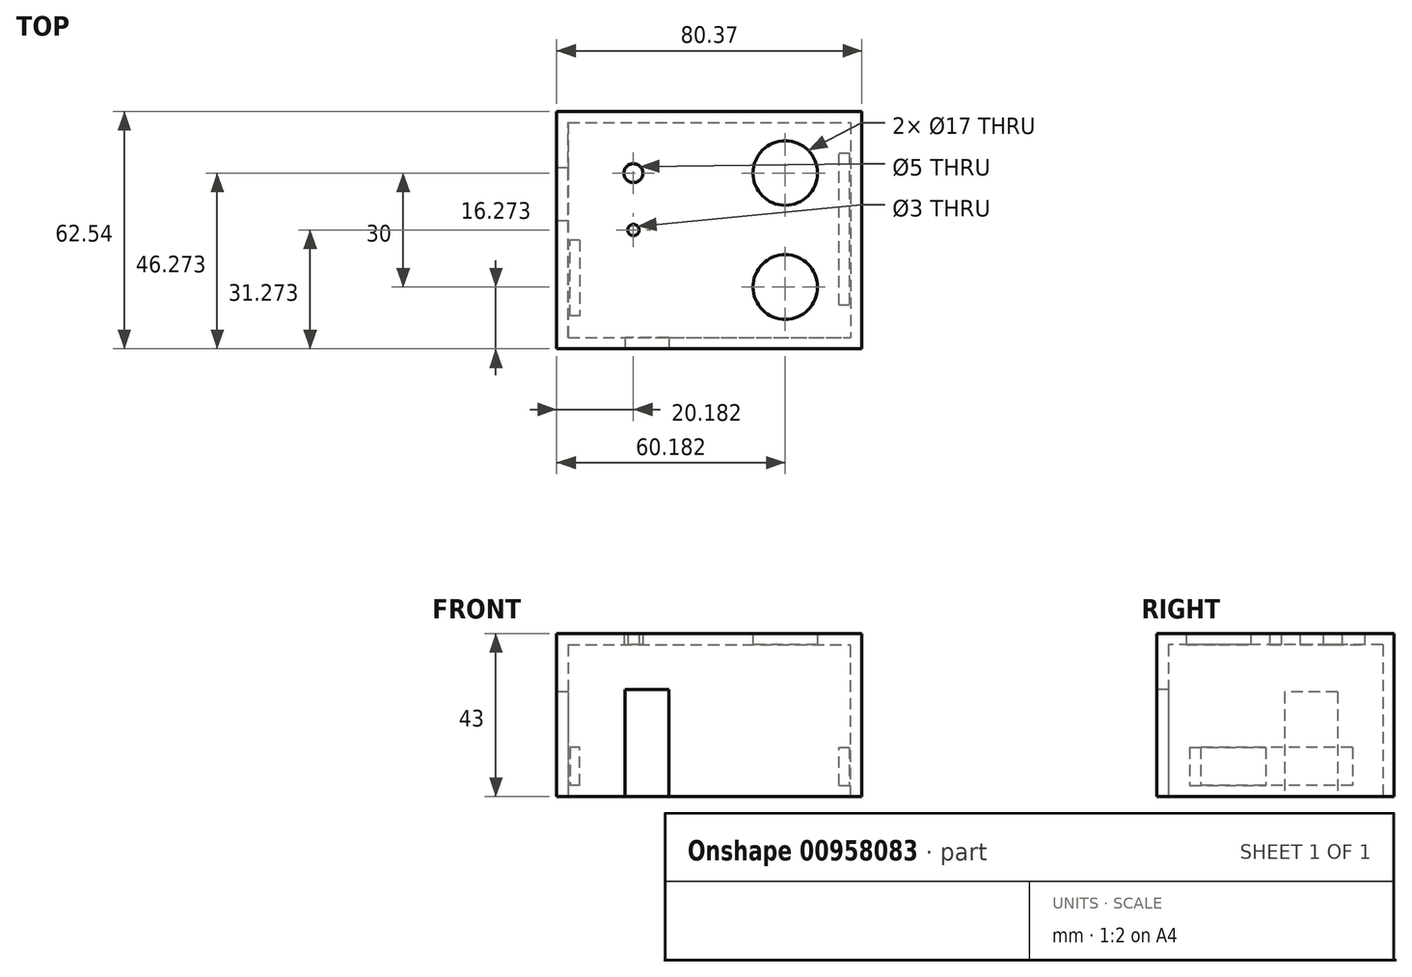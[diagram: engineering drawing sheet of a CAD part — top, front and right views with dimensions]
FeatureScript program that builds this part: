
annotation { "Feature Type Name" : "Feature", "Feature Type Description" : "" }
export const myFeature = defineFeature(function(context is Context, id is Id, definition is map)
    precondition{}
    {
        {
            var Q0;
            Q0=qCreatedBy(makeId("Top.planeOp"),FACE);
            var sketch = newSketch(context, id + "F0", { "sketchPlane" : qUnion([Q0])});
            skLineSegment(sketch, "E0.bottom", {"start": v(-70.32, 44.73) * mm, "end": v(10.05, 44.73) * mm});
            skLineSegment(sketch, "E0.top", {"start": v(-70.32, -17.8) * mm, "end": v(10.05, -17.8) * mm});
            skLineSegment(sketch, "E0.left", {"start": v(-70.32, 44.73) * mm, "end": v(-70.32, -17.8) * mm});
            skLineSegment(sketch, "E0.right", {"start": v(10.05, 44.73) * mm, "end": v(10.05, -17.8) * mm});
            skLineSegment(sketch, "E1", {"start": v(-30.14, 44.73) * mm, "end": v(-30.14, -17.8) * mm});
            skLineSegment(sketch, "E2", {"start": v(-70.32, 13.46) * mm, "end": v(10.05, 13.46) * mm});
            skLineSegment(sketch, "E3", {"start": v(-10.14, 44.73) * mm, "end": v(-10.14, -17.8) * mm});
            skLineSegment(sketch, "E4", {"start": v(-50.14, 44.73) * mm, "end": v(-50.14, -17.8) * mm});
            skLineSegment(sketch, "E5", {"start": v(-70.32, 28.46) * mm, "end": v(10.05, 28.46) * mm});
            skLineSegment(sketch, "E6", {"start": v(10.05, -1.54) * mm, "end": v(-70.32, -1.54) * mm});
            skCircle(sketch, "E7", {"center": v(-10.14, -1.54) * mm, "radius": 8.5 * mm});
            skCircle(sketch, "E8", {"center": v(-50.14, 28.46) * mm, "radius": 2.5 * mm});
            skCircle(sketch, "E9", {"center": v(-10.14, 28.46) * mm, "radius": 8.5 * mm});
            skCircle(sketch, "E10", {"center": v(-50.14, 13.46) * mm, "radius": 1.5 * mm});
            skSolve(sketch);
        }
        {
            var Q0;
            Q0=qSketchRegion(id+"F0",true);
            var Q1;
            {var subQ0=sQuery(id+"F0.wireOp",EDGE,"E5");var subQ1=sQuery(id+"F0.wireOp",EDGE,"E1");var subQ2=makeQuery(id+"F0.imprint","INTERSECT",VERTEX,{"derivedFrom":[subQ1,subQ0]});Q1=makeQuery(id+"F0.imprint","IMPRINT",FACE,{"disambiguationData":[TD([[makeQuery(id+"F0.imprint","IMPRINT",EDGE,{"disambiguationData":[TD([[subQ2,-1.0]])],"derivedFrom":subQ1}),-1.0]])]});}
            var Q2;
            {var subQ0=sQuery(id+"F0.wireOp",EDGE,"E5");var subQ1=sQuery(id+"F0.wireOp",EDGE,"E1");var subQ2=makeQuery(id+"F0.imprint","INTERSECT",VERTEX,{"derivedFrom":[subQ1,subQ0]});Q2=makeQuery(id+"F0.imprint","IMPRINT",FACE,{"disambiguationData":[TD([[makeQuery(id+"F0.imprint","IMPRINT",EDGE,{"disambiguationData":[TD([[subQ2,-1.0]])],"derivedFrom":subQ1}),1.0]])]});}
            var Q3;
            {var subQ1=sQuery(id+"F0.wireOp",EDGE,"E1");var subQ5=sQuery(id+"F0.wireOp",EDGE,"E2");var subQ6=makeQuery(id+"F0.imprint","INTERSECT",VERTEX,{"derivedFrom":[subQ1,subQ5]});Q3=makeQuery(id+"F0.imprint","IMPRINT",FACE,{"disambiguationData":[TD([[makeQuery(id+"F0.imprint","IMPRINT",EDGE,{"disambiguationData":[TD([[subQ6,-1.0]])],"derivedFrom":subQ1}),1.0]])]});}
            var Q4;
            {var subQ1=sQuery(id+"F0.wireOp",EDGE,"E2");var subQ5=sQuery(id+"F0.wireOp",EDGE,"E1");var subQ6=makeQuery(id+"F0.imprint","INTERSECT",VERTEX,{"derivedFrom":[subQ5,subQ1]});Q4=makeQuery(id+"F0.imprint","IMPRINT",FACE,{"disambiguationData":[TD([[makeQuery(id+"F0.imprint","IMPRINT",EDGE,{"disambiguationData":[TD([[subQ6,-1.0]])],"derivedFrom":subQ5}),-1.0]])]});}
            extrude(context, id + "F1", {"entities" : qUnion([Q0, Q1, Q2, Q3, Q4]), "depth" : 3 * mm, "offsetDistance" : 25 * mm});
        }
        {
            var Q0;
            {var subQ1=sQuery(id+"F0.wireOp",EDGE,"E0.top");var subQ5=sQuery(id+"F0.wireOp",EDGE,"E0.left");var subQ6=makeQuery(id+"F0.imprint","INTERSECT",VERTEX,{"derivedFrom":[subQ1,subQ5]});Q0=makeQuery(id+"F0.imprint","IMPRINT",FACE,{"disambiguationData":[TD([[makeQuery(id+"F0.imprint","IMPRINT",EDGE,{"disambiguationData":[TD([[subQ6,-1.0]])],"derivedFrom":subQ1}),1.0]])]});}
            var sketch = newSketch(context, id + "F2", { "sketchPlane" : qUnion([Q0])});
            skLineSegment(sketch, "E11.0", {"start": v(-67.32, -14.8) * mm, "end": v(7.05, -14.8) * mm});
            skLineSegment(sketch, "E11.1", {"start": v(-67.32, 41.73) * mm, "end": v(-67.32, -14.8) * mm});
            skLineSegment(sketch, "E11.2", {"start": v(-67.32, 41.73) * mm, "end": v(7.05, 41.73) * mm});
            skLineSegment(sketch, "E11.3", {"start": v(7.05, 41.73) * mm, "end": v(7.05, -14.8) * mm});
            skLineSegment(sketch, "E12.0", {"start": v(-70.32, -17.8) * mm, "end": v(10.05, -17.8) * mm});
            skLineSegment(sketch, "E12.1", {"start": v(-70.32, 44.73) * mm, "end": v(-70.32, -17.8) * mm});
            skLineSegment(sketch, "E12.2", {"start": v(-70.32, 44.73) * mm, "end": v(10.05, 44.73) * mm});
            skLineSegment(sketch, "E12.3", {"start": v(10.05, 44.73) * mm, "end": v(10.05, -17.8) * mm});
            skSolve(sketch);
        }
        {
            var Q0;
            {var subQ10=sQuery(id+"F2.wireOp",EDGE,"E11.1");var subQ11=sQuery(id+"F2.wireOp",EDGE,"E11.0");var subQ12=makeQuery(id+"F2.imprint","INTERSECT",VERTEX,{"derivedFrom":[subQ11,subQ10]});Q0=makeQuery(id+"F2.imprint","IMPRINT",FACE,{"disambiguationData":[TD([[makeQuery(id+"F2.imprint","IMPRINT",EDGE,{"disambiguationData":[TD([[subQ12,-1.0]])],"derivedFrom":subQ11}),-1.0]])]});}
            var Q1;
            {var subQ1=sQuery(id+"F2.wireOp",EDGE,"E11.2");Q1=makeQuery(id+"F2.imprint","IMPRINT",FACE,{"disambiguationData":[TD([[makeQuery(id+"F2.imprint","IMPRINT",EDGE,{"derivedFrom":subQ1}),1.0]])]});}
            extrude(context, id + "F3", {"entities" : qUnion([Q0, Q1]), "oppositeDirection" : true, "depth" : 40 * mm, "offsetDistance" : 25 * mm});
        }
        {
            var Q0;
            Q0=makeQuery(id+"F3.boolean.opBoolean","MERGE",FACE,{"derivedFrom":[makeQuery(id+"F1.opExtrude","SWEPT_FACE",FACE,{"disambiguationData":[OSD([sQuery(id+"F0.wireOp",EDGE,"E0.left")])]}),makeQuery(id+"F3.opExtrude","SWEPT_FACE",FACE,{"disambiguationData":[OSD([sQuery(id+"F2.wireOp",EDGE,"E12.1")])]})]});
            var sketch = newSketch(context, id + "F4", { "sketchPlane" : qUnion([Q0])});
            skLineSegment(sketch, "E13.bottom", {"start": v(-29.83, -12.4) * mm, "end": v(-15.83, -12.4) * mm});
            skLineSegment(sketch, "E13.top", {"start": v(-29.83, -29) * mm, "end": v(-15.83, -29) * mm});
            skLineSegment(sketch, "E13.left", {"start": v(-29.83, -12.4) * mm, "end": v(-29.83, -29) * mm});
            skLineSegment(sketch, "E13.right", {"start": v(-15.83, -12.4) * mm, "end": v(-15.83, -29) * mm});
            skLineSegment(sketch, "E14.top", {"start": v(-9.2, -26.4) * mm, "end": v(2.8, -26.4) * mm});
            skLineSegment(sketch, "E14.left", {"start": v(-9.2, -19.4) * mm, "end": v(-9.2, -26.4) * mm});
            skLineSegment(sketch, "E14.right", {"start": v(2.8, -19.4) * mm, "end": v(2.8, -26.4) * mm});
            skLineSegment(sketch, "E15", {"start": v(-9.2, -26.4) * mm, "end": v(-15.83, -26.4) * mm});
            skSolve(sketch);
        }
        {
            var Q0;
            Q0=makeQuery(id+"F4.imprint","IMPRINT",FACE,{"disambiguationData":[TD([[makeQuery(id+"F4.imprint","IMPRINT",EDGE,{"derivedFrom":sQuery(id+"F4.wireOp",EDGE,"E13.bottom")}),-1.0]])]});
            var Q1;
            Q1=makeQuery(id+"F4.imprint","IMPRINT",FACE,{"disambiguationData":[TD([[makeQuery(id+"F4.imprint","IMPRINT",EDGE,{"derivedFrom":sQuery(id+"F4.wireOp",EDGE,"E14.bottom")}),-1.0]])]});
            var Q2;
            Q2=makeQuery(id+"F4.imprint","IMPRINT",FACE,{"disambiguationData":[TD([[makeQuery(id+"F4.imprint","IMPRINT",EDGE,{"derivedFrom":sQuery(id+"F4.wireOp",EDGE,"E14.left")}),-1.0]])]});
            extrude(context, id + "F5", {"entities" : qUnion([Q0, Q1, Q2]), "operationType" : NewBodyOperationType.REMOVE, "oppositeDirection" : true, "depth" : 25 * mm, "offsetDistance" : 25 * mm});
        }
        {
            var Q0;
            Q0=makeQuery(id+"F5.boolean.opBoolean","COPY",FACE,{"derivedFrom":makeQuery(id+"F5.opExtrude","SWEPT_FACE",FACE,{"disambiguationData":[OSD([sQuery(id+"F4.wireOp",EDGE,"E13.top")])]})});
            var Q1;
            Q1=makeQuery(id+"F5.boolean.opBoolean","COPY",FACE,{"derivedFrom":makeQuery(id+"F5.opExtrude","SWEPT_FACE",FACE,{"disambiguationData":[OSD([sQuery(id+"F4.wireOp",EDGE,"E14.top")])]})});
            extrude(context, id + "F6", {"entities" : qUnion([Q0, Q1]), "operationType" : NewBodyOperationType.REMOVE, "endBound" : BoundingType.THROUGH_ALL, "oppositeDirection" : true, "depth" : 25 * mm, "offsetDistance" : 25 * mm});
        }
        {
            var Q0;
            Q0=makeQuery(id+"F3.boolean.opBoolean","MERGE",FACE,{"derivedFrom":[makeQuery(id+"F1.opExtrude","SWEPT_FACE",FACE,{"disambiguationData":[OSD([sQuery(id+"F0.wireOp",EDGE,"E0.top")])]}),makeQuery(id+"F3.opExtrude","SWEPT_FACE",FACE,{"disambiguationData":[OSD([sQuery(id+"F2.wireOp",EDGE,"E12.0")])]})]});
            var sketch = newSketch(context, id + "F7", { "sketchPlane" : qUnion([Q0])});
            skLineSegment(sketch, "E16.bottom", {"start": v(-40.82, -111.8) * mm, "end": v(-52.32, -111.8) * mm});
            skLineSegment(sketch, "E16.top", {"start": v(-40.82, -11.8) * mm, "end": v(-52.32, -11.8) * mm});
            skLineSegment(sketch, "E16.left", {"start": v(-52.32, -11.8) * mm, "end": v(-52.32, -111.8) * mm});
            skLineSegment(sketch, "E16.right", {"start": v(-40.82, -11.8) * mm, "end": v(-40.82, -111.8) * mm});
            skSolve(sketch);
        }
        {
            var Q0;
            Q0=qSketchRegion(id+"F7",true);
            var Q1;
            {var subQ0=sQuery(id+"F7.wireOp",EDGE,"E16.bottom");Q1=makeQuery(id+"F7.imprint","IMPRINT",FACE,{"disambiguationData":[TD([[makeQuery(id+"F7.imprint","IMPRINT",EDGE,{"derivedFrom":subQ0}),-1.0]])]});}
            extrude(context, id + "F8", {"entities" : qUnion([Q0, Q1]), "operationType" : NewBodyOperationType.REMOVE, "oppositeDirection" : true, "depth" : 5.1 * mm, "offsetDistance" : 25 * mm});
        }
        {
            var Q0;
            Q0=makeQuery(id+"F3.opExtrude","SWEPT_FACE",FACE,{"disambiguationData":[OSD([sQuery(id+"F2.wireOp",EDGE,"E11.1")])]});
            var sketch = newSketch(context, id + "F9", { "sketchPlane" : qUnion([Q0])});
            skLineSegment(sketch, "E17.bottom", {"start": v(10.83, -37) * mm, "end": v(-9.17, -37) * mm});
            skLineSegment(sketch, "E17.top", {"start": v(10.83, -27) * mm, "end": v(-9.17, -27) * mm});
            skLineSegment(sketch, "E17.left", {"start": v(10.83, -37) * mm, "end": v(10.83, -27) * mm});
            skLineSegment(sketch, "E17.right", {"start": v(-9.17, -37) * mm, "end": v(-9.17, -27) * mm});
            skSolve(sketch);
        }
        {
            var Q0;
            Q0=makeQuery(id+"F9.imprint","IMPRINT",FACE,{"disambiguationData":[TD([[makeQuery(id+"F9.imprint","IMPRINT",EDGE,{"derivedFrom":sQuery(id+"F9.wireOp",EDGE,"E17.bottom")}),-1.0]])]});
            extrude(context, id + "F10", {"entities" : qUnion([Q0]), "depth" : 3 * mm, "offsetDistance" : 25 * mm});
        }
        {
            var Q0;
            Q0=makeQuery(id+"F3.opExtrude","SWEPT_FACE",FACE,{"disambiguationData":[OSD([sQuery(id+"F2.wireOp",EDGE,"E11.3")])]});
            var sketch = newSketch(context, id + "F11", { "sketchPlane" : qUnion([Q0])});
            skLineSegment(sketch, "E18.bottom", {"start": v(6.27, -37) * mm, "end": v(-33.73, -37) * mm});
            skLineSegment(sketch, "E18.top", {"start": v(6.27, -27) * mm, "end": v(-33.73, -27) * mm});
            skLineSegment(sketch, "E18.left", {"start": v(6.27, -37) * mm, "end": v(6.27, -27) * mm});
            skLineSegment(sketch, "E18.right", {"start": v(-33.73, -37) * mm, "end": v(-33.73, -27) * mm});
            skSolve(sketch);
        }
        {
            var Q0;
            Q0 = qSketchRegion(id + "F11", true);
            extrude(context, id + "F12", {"entities" : qUnion([Q0]), "depth" : 3 * mm, "offsetDistance" : 25 * mm});
        }
        {
            var Q0;
            Q0=makeQuery(id+"F3.opExtrude","SWEPT_FACE",FACE,{"disambiguationData":[OSD([sQuery(id+"F2.wireOp",EDGE,"E12.2")])]});
            var sketch = newSketch(context, id + "F13", { "sketchPlane" : qUnion([Q0])});
            skLineSegment(sketch, "E19", {"start": v(-7.05, 0) * mm, "end": v(-7.05, -40) * mm});
            skLineSegment(sketch, "E20", {"start": v(-6.75, 0) * mm, "end": v(-6.75, -40) * mm});
            skLineSegment(sketch, "E21", {"start": v(67.32, 0) * mm, "end": v(67.32, -40) * mm});
            skLineSegment(sketch, "E22", {"start": v(67.32, -40) * mm, "end": v(66.82, -40) * mm});
            skLineSegment(sketch, "E23", {"start": v(66.82, -40) * mm, "end": v(66.82, 0) * mm});
            skSolve(sketch);
        }
        {
            var Q0;
            {var subQ0=sQuery(id+"F13.wireOp",EDGE,"E19");Q0=makeQuery(id+"F13.imprint","IMPRINT",FACE,{"disambiguationData":[TD([[makeQuery(id+"F13.imprint","IMPRINT",EDGE,{"derivedFrom":subQ0}),1.0]])]});}
            var Q1;
            {var subQ0=sQuery(id+"F13.wireOp",EDGE,"E21");Q1=makeQuery(id+"F13.imprint","IMPRINT",FACE,{"disambiguationData":[TD([[makeQuery(id+"F13.imprint","IMPRINT",EDGE,{"derivedFrom":subQ0}),-1.0]])]});}
            extrude(context, id + "F14", {"entities" : qUnion([Q0, Q1]), "operationType" : NewBodyOperationType.REMOVE, "endBound" : BoundingType.THROUGH_ALL, "oppositeDirection" : true, "depth" : 25 * mm, "offsetDistance" : 25 * mm});
        }
        {
            var Q0;
            {var subQ5=sQuery(id+"F2.wireOp",EDGE,"E11.2");Q0=makeQuery(id+"F14.boolean.opBoolean","COPY",FACE,{"disambiguationData":[TD([makeQuery(id+"F3.opExtrude","SWEPT_FACE",FACE,{"disambiguationData":[OSD([subQ5])]})])],"derivedFrom":makeQuery(id+"F14.opExtrude","SWEPT_FACE",FACE,{"disambiguationData":[OSD([sQuery(id+"F13.wireOp",EDGE,"E23")])]})});}
            var Q1;
            {var subQ0=sQuery(id+"F2.wireOp",EDGE,"E11.0");Q1=makeQuery(id+"F14.boolean.opBoolean","COPY",FACE,{"disambiguationData":[TD([makeQuery(id+"F3.opExtrude","SWEPT_FACE",FACE,{"disambiguationData":[OSD([subQ0])]})])],"derivedFrom":makeQuery(id+"F14.opExtrude","SWEPT_FACE",FACE,{"disambiguationData":[OSD([sQuery(id+"F13.wireOp",EDGE,"E23")])]})});}
            extrude(context, id + "F15", {"entities" : qUnion([Q0, Q1]), "operationType" : NewBodyOperationType.ADD, "depth" : 0.5 * mm, "offsetDistance" : 25 * mm});
        }
        {
            var Q0;
            {var subQ5=sQuery(id+"F2.wireOp",EDGE,"E11.2");Q0=makeQuery(id+"F14.boolean.opBoolean","COPY",FACE,{"disambiguationData":[TD([makeQuery(id+"F3.opExtrude","SWEPT_FACE",FACE,{"disambiguationData":[OSD([subQ5])]})])],"derivedFrom":makeQuery(id+"F14.opExtrude","SWEPT_FACE",FACE,{"disambiguationData":[OSD([sQuery(id+"F13.wireOp",EDGE,"E20")])]})});}
            var Q1;
            {var subQ0=sQuery(id+"F2.wireOp",EDGE,"E11.0");Q1=makeQuery(id+"F14.boolean.opBoolean","COPY",FACE,{"disambiguationData":[TD([makeQuery(id+"F3.opExtrude","SWEPT_FACE",FACE,{"disambiguationData":[OSD([subQ0])]})])],"derivedFrom":makeQuery(id+"F14.opExtrude","SWEPT_FACE",FACE,{"disambiguationData":[OSD([sQuery(id+"F13.wireOp",EDGE,"E20")])]})});}
            extrude(context, id + "F16", {"entities" : qUnion([Q0, Q1]), "operationType" : NewBodyOperationType.ADD, "depth" : 0.5 * mm, "offsetDistance" : 25 * mm});
        }
    });
